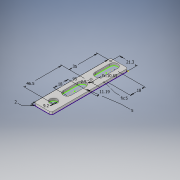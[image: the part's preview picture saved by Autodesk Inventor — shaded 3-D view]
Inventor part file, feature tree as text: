
AUTODESK INVENTOR PART (.ipt)
format: ipt  version: 2019 (Build 230136000, 136)  size: 135,168 bytes
history: native  units: mm
features: extrude x2, sketch x1
ambient origin geometry x8: Origin, YZ Plane, XZ Plane, XY Plane, X Axis, Y Axis, Z Axis, Center Point
bodies: Solid1 (feature_tree)
feature tree (3):
  sketch  "Sketch1"  dims[d0=21.3mm d1=95.0mm d2=2.5mm d3=35.0mm d6=10.65mm d8=2.0mm d9=9.2mm d10=46.5mm d11=3.0mm d12=0.0mm d13=18.0mm d14=5.0mm d15=10.0mm d16=0.0mm d17=11.189852mm d18=18.0mm d19=5.0mm]
  extrude  "Extrusion1"  Depth=95.0mm
  extrude  "Extrusion2"  Depth=5.0mm
